# Revit family: 33-HC_RAV_HCL_TOSHIBA_RM1CTP_80
name_source: partatom
category: Mechanical Equipment
revit_build: Autodesk Revit 2017 (Build: 20160225_1515(x64)
units: mm (PartAtom-declared; Revit-internal decimal feet)

## family parameters
Always vertical = Yes
Cut with Voids When Loaded = No
OmniClass Number = 23.75.00.00
OmniClass Title = Climate Control (HVAC)
Part Type = Normal
Room Calculation Point = No
Round Connector Dimension = Use Diameter
Shared = No
Work Plane-Based = No

## types (1)
- RAV-RM801CTP-E
    Air filter = Long life filter
    Airflow (m3/h) = 1410
    Article Description = R32 Ceiling
    Article Type = RAV-RM801CTP-E
    Casing material = -
    Content Supplier URL = www.hcltech.com
    Depth (mm) = 690 mm  [stored 2.26378 ft]
    Description = R32 Ceiling
    Drain Pipe Diameter (mm) = 26 mm
    Duct diameter (mm) = -
    EMCS = 4
    ETIM Article Class = EC001213
    Energy Class-Cooling/Heating = A+ / A+
    Frequency (Hz) = 50
    Height (mm) = 235 mm
    Hydronic Return Diameter (mm) = 16 mm  [stored 0.0524934 ft]
    Hydronic Supply Diameter (mm) = 10 mm  [stored 0.0328084 ft]
    MCA (A) = -
    MEPcontent Class = HEATPUMP
    MOCP (A) = 25
    Manufacturer = Toshiba
    Manufacturer Art. No. = RAV-RM801CTP-E
    Manufacturer URL = https://www.toshiba-carrier.co.jp
    Model = RAV-RM801CTP-E
    Operating range - Cooling (°C) = 21 - 32
    Operating range - Heating (°C) = 0 - 28
    Part load = -
    Pdesign-Cooling/Heating = 6.9 / 5.1
    Piping connection = Flare
    Power consumption-Cooling (Kw) = 1.6
    Power consumption-Heating (Kw) = 1.8
    Product Line = TCTC
    Rated Capacities - Cooling/Heating (kW) = 6.9 / 7.7
    Rated Power Consumption = 2.38 / 2.13
    Rated efficiency-EER/COP = 2.90 / 3.62
    Red = Colour RGB-250 000 000
    Refrigerant Information = R32 / R410A
    Revit Version = 2017
    Running current-Cooling (A) = 7.82 - 7.17
    Running current-Heating (A) = 8.70 - 7.98
    Seasonal & Rated efficiency-SEER/SCOP = 5.62 / 4.21
    Sound pressure - High (dB) = 41
    Sound pressure - Low (dB) = 29
    Sound pressure - Mid (dB) = 36
    Starting current (A) = 15.5
    Static pressure (Pa) = -
    URL = https://www.toshiba-carrier.co.jp
    Voltage (V) = 220-240
    Weight (Kg) = 23
    White = Colour- RGB 255 255  255
    Width (mm) = 1270 mm

note: [stored X ft] marks values corroborated as IEEE doubles in the binary element streams (Revit-internal decimal feet)

## geometry (parser evidence)
native form markers: Sweep x5
no freeform markers — native parametric forms only
